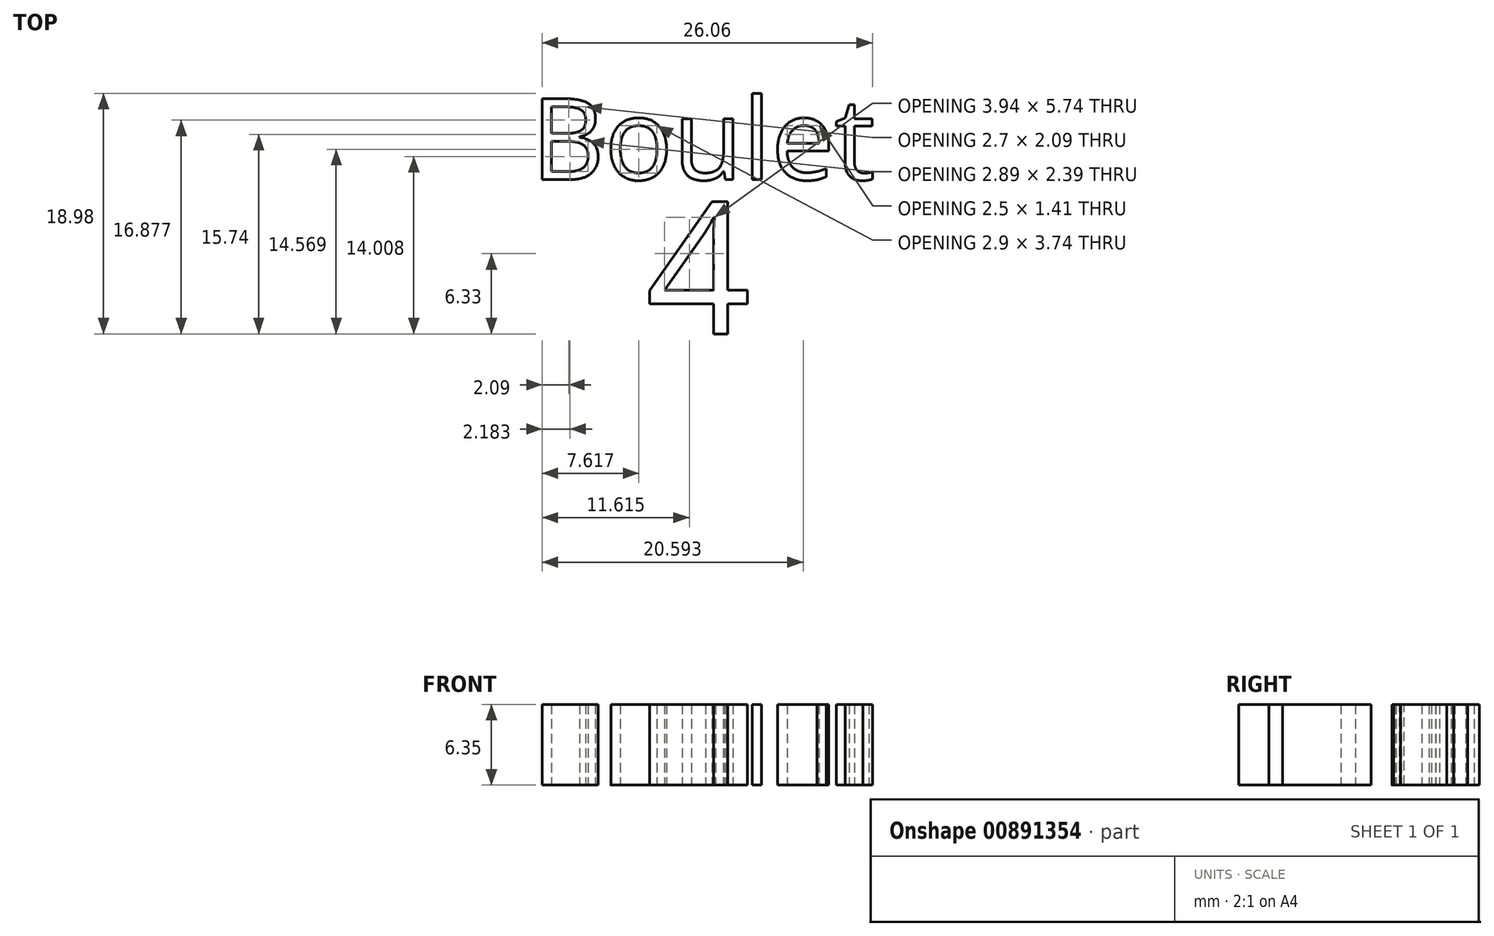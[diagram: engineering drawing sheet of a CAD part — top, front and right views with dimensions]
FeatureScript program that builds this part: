
annotation { "Feature Type Name" : "Feature", "Feature Type Description" : "" }
export const myFeature = defineFeature(function(context is Context, id is Id, definition is map)
    precondition{}
    {
        {
            var Q0;
            Q0=qCreatedBy(makeId("Top.planeOp"),FACE);
            var sketch = newSketch(context, id + "F0", { "sketchPlane" : qUnion([Q0])});
            skText(sketch, "E0", { "text": "Boulet", "fontName": "OpenSans-Regular.ttf"});
            const initialGuessF0  = {"E0": [-0.03464, 0.02635, 1, 0, 0.00644]};
            skSetInitialGuess(sketch, initialGuessF0);
            skSolve(sketch);
        }
        {
            var Q0;
            Q0=qCreatedBy(makeId("Top.planeOp"),FACE);
            var sketch = newSketch(context, id + "F1", { "sketchPlane" : qUnion([Q0])});
            skText(sketch, "E1", { "text": "4\n", "fontName": "OpenSans-Regular.ttf"});
            const initialGuessF1  = {"E1": [-0.0256, 0.01417, 1, 0, 0.01047]};
            skSetInitialGuess(sketch, initialGuessF1);
            skSolve(sketch);
        }
        {
            var Q0;
            Q0 = qSketchRegion(id + "F0", true);
            extrude(context, id + "F2", {"entities" : qUnion([Q0]), "depth" : 6.35 * mm, "offsetDistance" : 25.4 * mm});
        }
        {
            var Q0;
            Q0 = qSketchRegion(id + "F1", true);
            extrude(context, id + "F3", {"entities" : qUnion([Q0]), "depth" : 6.35 * mm, "offsetDistance" : 25.4 * mm});
        }
    });
